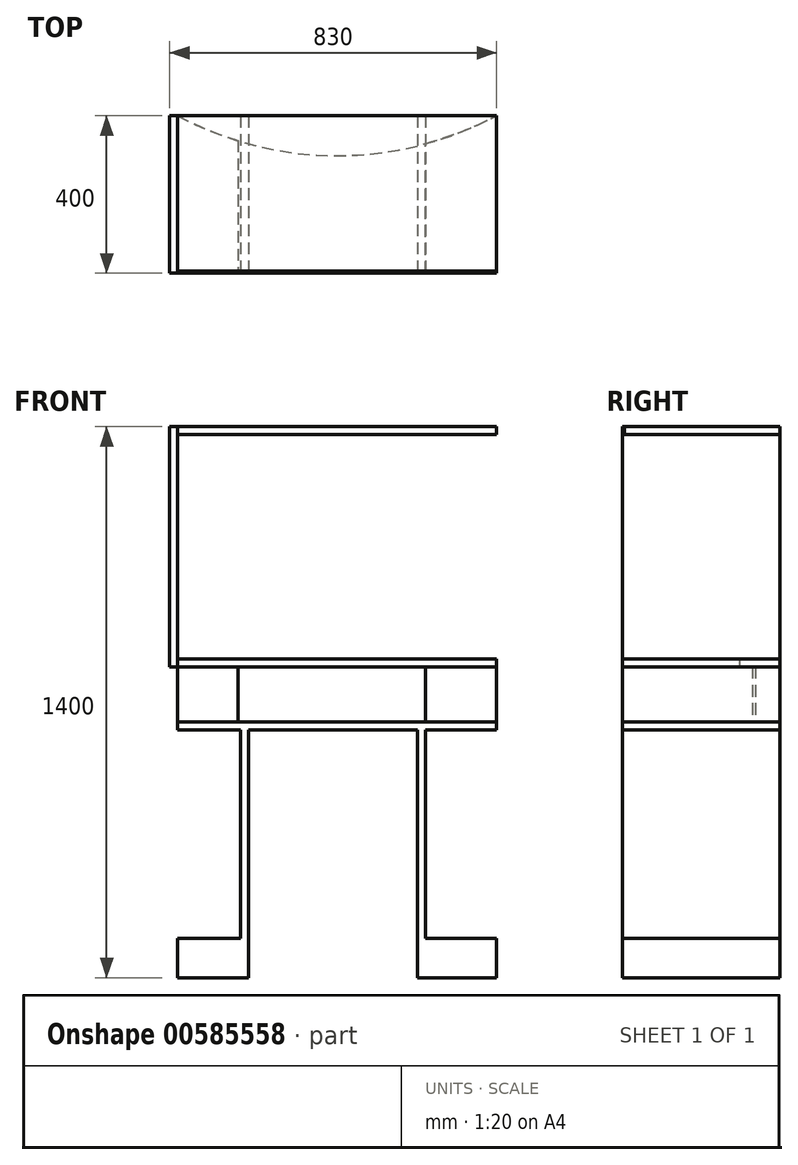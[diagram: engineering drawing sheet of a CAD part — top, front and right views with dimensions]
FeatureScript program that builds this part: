
annotation { "Feature Type Name" : "Feature", "Feature Type Description" : "" }
export const myFeature = defineFeature(function(context is Context, id is Id, definition is map)
    precondition{}
    {
        {
            var Q0;
            Q0=qCreatedBy(makeId("Front.planeOp"),FACE);
            var sketch = newSketch(context, id + "F0", { "sketchPlane" : qUnion([Q0])});
            skLineSegment(sketch, "E0.bottom", {"start": v(-650, -795.62) * mm, "end": v(200, -795.62) * mm});
            skLineSegment(sketch, "E0.top", {"start": v(-650, 604.38) * mm, "end": v(200, 604.38) * mm});
            skLineSegment(sketch, "E0.left", {"start": v(-650, -795.62) * mm, "end": v(-650, 604.38) * mm});
            skLineSegment(sketch, "E0.right", {"start": v(200, -795.62) * mm, "end": v(200, 604.38) * mm});
            skLineSegment(sketch, "E1.left", {"start": v(-650, 604.38) * mm, "end": v(-650, 534.38) * mm});
            skLineSegment(sketch, "E2", {"start": v(200, 604.38) * mm, "end": v(200, -795.62) * mm});
            skLineSegment(sketch, "E3", {"start": v(180, 604.38) * mm, "end": v(180, -795.62) * mm});
            skPoint(sketch, "E4.start.orphan", {"position": v(137.97, 604.38) * mm});
            skPoint(sketch, "E5.start.orphan", {"position": v(-630, 534.38) * mm});
            skLineSegment(sketch, "E6", {"start": v(180, -145.62) * mm, "end": v(-630, -145.62) * mm});
            skLineSegment(sketch, "E7", {"start": v(-630, -795.62) * mm, "end": v(-630, -145.62) * mm});
            skPoint(sketch, "E8.orphan", {"position": v(-610, 534.38) * mm});
            skLineSegment(sketch, "E9", {"start": v(-630, -145.62) * mm, "end": v(-630, 534.38) * mm});
            skLineSegment(sketch, "E10", {"start": v(-630, -165.62) * mm, "end": v(180, -165.62) * mm});
            skLineSegment(sketch, "E11", {"start": v(-630, -695.62) * mm, "end": v(180, -695.62) * mm});
            skLineSegment(sketch, "E12", {"start": v(-20, -795.62) * mm, "end": v(-20, -165.62) * mm});
            skLineSegment(sketch, "E13", {"start": v(0, -165.62) * mm, "end": v(0, -695.62) * mm});
            skLineSegment(sketch, "E14", {"start": v(-450, -165.62) * mm, "end": v(-450, -795.62) * mm});
            skLineSegment(sketch, "E15", {"start": v(-470, -165.62) * mm, "end": v(-470, -795.62) * mm});
            skLineSegment(sketch, "E16", {"start": v(0, -695.62) * mm, "end": v(0, -795.62) * mm});
            skLineSegment(sketch, "E17", {"start": v(180, 14.38) * mm, "end": v(-630, 14.38) * mm});
            skPoint(sketch, "E17.endSnap0", {"position": v(-630, 194.38) * mm});
            skLineSegment(sketch, "E18", {"start": v(-630, -5.62) * mm, "end": v(180, -5.62) * mm});
            skPoint(sketch, "E18.endSnap0", {"position": v(180, -95.62) * mm});
            skPoint(sketch, "E19.end.orphan", {"position": v(-590, 534.38) * mm});
            skLineSegment(sketch, "E20", {"start": v(-630, 534.38) * mm, "end": v(-630, 604.38) * mm});
            skLineSegment(sketch, "E21.top", {"start": v(-650, -5.62) * mm, "end": v(200, -5.62) * mm});
            skLineSegment(sketch, "E21.left", {"start": v(-650, 604.38) * mm, "end": v(-650, -5.62) * mm});
            skLineSegment(sketch, "E21.right", {"start": v(200, 604.38) * mm, "end": v(200, -5.62) * mm});
            skSolve(sketch);
        }
        {
            var Q0;
            {var subQ0=sQuery(id+"F0.wireOp",EDGE,"E14");var subQ1=sQuery(id+"F0.wireOp",EDGE,"E10");var subQ2=makeQuery(id+"F0.imprint","INTERSECT",VERTEX,{"derivedFrom":[subQ1,subQ0]});Q0=makeQuery(id+"F0.imprint","IMPRINT",FACE,{"disambiguationData":[TD([[makeQuery(id+"F0.imprint","IMPRINT",EDGE,{"disambiguationData":[TD([[subQ2,1.0]])],"derivedFrom":subQ1}),-1.0]])]});}
            var Q1;
            {var subQ3=sQuery(id+"F0.wireOp",EDGE,"E13");Q1=makeQuery(id+"F0.imprint","IMPRINT",FACE,{"disambiguationData":[TD([[makeQuery(id+"F0.imprint","IMPRINT",EDGE,{"derivedFrom":subQ3}),-1.0]])]});}
            var Q2;
            {var subQ1=sQuery(id+"F0.wireOp",EDGE,"E6");Q2=makeQuery(id+"F0.imprint","IMPRINT",FACE,{"disambiguationData":[TD([[makeQuery(id+"F0.imprint","IMPRINT",EDGE,{"derivedFrom":subQ1}),1.0]])]});}
            var Q3;
            {var subQ0=sQuery(id+"F0.wireOp",EDGE,"E7");var subQ1=sQuery(id+"F0.wireOp",EDGE,"E0.bottom");var subQ2=makeQuery(id+"F0.imprint","INTERSECT",VERTEX,{"derivedFrom":[subQ1,subQ0]});Q3=makeQuery(id+"F0.imprint","IMPRINT",FACE,{"disambiguationData":[TD([[makeQuery(id+"F0.imprint","IMPRINT",EDGE,{"disambiguationData":[TD([[subQ2,-1.0]])],"derivedFrom":subQ1}),1.0]])]});}
            var Q4;
            {var subQ0=sQuery(id+"F0.wireOp",EDGE,"E14");var subQ1=sQuery(id+"F0.wireOp",EDGE,"E0.bottom");var subQ2=makeQuery(id+"F0.imprint","INTERSECT",VERTEX,{"derivedFrom":[subQ1,subQ0]});Q4=makeQuery(id+"F0.imprint","IMPRINT",FACE,{"disambiguationData":[TD([[makeQuery(id+"F0.imprint","IMPRINT",EDGE,{"disambiguationData":[TD([[subQ2,1.0]])],"derivedFrom":subQ1}),1.0]])]});}
            var Q5;
            {var subQ3=sQuery(id+"F0.wireOp",EDGE,"E16");Q5=makeQuery(id+"F0.imprint","IMPRINT",FACE,{"disambiguationData":[TD([[makeQuery(id+"F0.imprint","IMPRINT",EDGE,{"derivedFrom":subQ3}),-1.0]])]});}
            var Q6;
            {var subQ3=sQuery(id+"F0.wireOp",EDGE,"E16");Q6=makeQuery(id+"F0.imprint","IMPRINT",FACE,{"disambiguationData":[TD([[makeQuery(id+"F0.imprint","IMPRINT",EDGE,{"derivedFrom":subQ3}),1.0]])]});}
            var Q7;
            {var subQ5=sQuery(id+"F0.wireOp",EDGE,"E0.left");Q7=makeQuery(id+"F0.imprint","IMPRINT",FACE,{"disambiguationData":[TD([[makeQuery(id+"F0.imprint","IMPRINT",EDGE,{"derivedFrom":subQ5}),-1.0]])]});}
            var Q8;
            {var subQ4=sQuery(id+"F0.wireOp",EDGE,"E2");Q8=makeQuery(id+"F0.imprint","IMPRINT",FACE,{"disambiguationData":[TD([[makeQuery(id+"F0.imprint","IMPRINT",EDGE,{"derivedFrom":subQ4}),-1.0]])]});}
            extrude(context, id + "F1", {"entities" : qUnion([Q0, Q1, Q2, Q3, Q4, Q5, Q6, Q7, Q8]), "oppositeDirection" : true, "depth" : 400 * mm, "offsetDistance" : 25.4 * mm});
        }
        {
            var Q0;
            Q0=makeQuery(id+"F1.opExtrude","SWEPT_FACE",FACE,{"disambiguationData":[OSD([sQuery(id+"F0.wireOp",EDGE,"E9"),sQuery(id+"F0.wireOp",EDGE,"E20")])]});
            var sketch = newSketch(context, id + "F2", { "sketchPlane" : qUnion([Q0])});
            skLineSegment(sketch, "E22.bottom", {"start": v(5.08, 584.38) * mm, "end": v(400, 584.38) * mm});
            skLineSegment(sketch, "E22.top", {"start": v(5.08, 604.38) * mm, "end": v(400, 604.38) * mm});
            skLineSegment(sketch, "E22.left", {"start": v(5.08, 584.38) * mm, "end": v(5.08, 604.38) * mm});
            skLineSegment(sketch, "E22.right", {"start": v(400, 584.38) * mm, "end": v(400, 604.38) * mm});
            skSolve(sketch);
        }
        {
            var Q0;
            {var subQ7=sQuery(id+"F2.wireOp",EDGE,"E22.bottom");Q0=makeQuery(id+"F2.imprint","IMPRINT",FACE,{"disambiguationData":[TD([[makeQuery(id+"F2.imprint","IMPRINT",EDGE,{"derivedFrom":subQ7}),1.0]])]});}
            extrude(context, id + "F3", {"entities" : qUnion([Q0]), "operationType" : NewBodyOperationType.ADD, "depth" : 810 * mm, "offsetDistance" : 25.4 * mm});
        }
        {
            var Q0;
            {var subQ0=sQuery(id+"F0.wireOp",EDGE,"E21.right");Q0=makeQuery(id+"F0.imprint","IMPRINT",FACE,{"disambiguationData":[TD([[makeQuery(id+"F0.imprint","IMPRINT",EDGE,{"derivedFrom":subQ0}),-1.0]])]});}
            var Q1;
            {var subQ1=sQuery(id+"F0.wireOp",EDGE,"E20");Q1=makeQuery(id+"F0.imprint","IMPRINT",FACE,{"disambiguationData":[TD([[makeQuery(id+"F0.imprint","IMPRINT",EDGE,{"derivedFrom":subQ1}),1.0]])]});}
            extrude(context, id + "F4", {"entities" : qUnion([Q0, Q1]), "oppositeDirection" : true, "depth" : 400 * mm, "offsetDistance" : 25.4 * mm});
        }
        {
            var Q0;
            {var subQ0=sQuery(id+"F0.wireOp",EDGE,"E17");Q0=makeQuery(id+"F0.imprint","IMPRINT",FACE,{"disambiguationData":[TD([[makeQuery(id+"F0.imprint","IMPRINT",EDGE,{"derivedFrom":subQ0}),-1.0]])]});}
            var sketch = newSketch(context, id + "F5", { "sketchPlane" : qUnion([Q0])});
            skSolve(sketch);
        }
        {
            var Q0;
            Q0 = qSketchRegion(id + "F5", true);
            var Q1;
            {var subQ0=sQuery(id+"F0.wireOp",EDGE,"E17");Q1=makeQuery(id+"F0.imprint","IMPRINT",FACE,{"disambiguationData":[TD([[makeQuery(id+"F0.imprint","IMPRINT",EDGE,{"derivedFrom":subQ0}),-1.0]])]});}
            extrude(context, id + "F6", {"entities" : qUnion([Q0, Q1]), "depth" : 20 * mm, "offsetDistance" : 25.4 * mm});
        }
        {
            var Q0;
            {var subQ0=sQuery(id+"F0.wireOp",EDGE,"E17");Q0=makeQuery(id+"F0.imprint","IMPRINT",FACE,{"disambiguationData":[TD([[makeQuery(id+"F0.imprint","IMPRINT",EDGE,{"derivedFrom":subQ0}),1.0]])]});}
            extrude(context, id + "F7", {"entities" : qUnion([Q0]), "oppositeDirection" : true, "depth" : 400 * mm, "offsetDistance" : 25.4 * mm});
        }
        {
            var Q0;
            Q0=makeQuery(id+"F7.opExtrude","SWEPT_FACE",FACE,{"disambiguationData":[OSD([sQuery(id+"F0.wireOp",EDGE,"E17")])]});
            var sketch = newSketch(context, id + "F8", { "sketchPlane" : qUnion([Q0])});
            skArc(sketch, "E23", {"start": v(-630, 400) * mm, "mid": v(-225, 298.46) * mm, "end": v(180, 400) * mm});
            skLineSegment(sketch, "E24", {"start": v(180, 400) * mm, "end": v(-630, 400) * mm});
            skSolve(sketch);
        }
        {
            var Q0;
            Q0=makeQuery(id+"F8.imprint","IMPRINT",FACE,{"disambiguationData":[TD([[makeQuery(id+"F8.imprint","IMPRINT",EDGE,{"derivedFrom":sQuery(id+"F8.wireOp",EDGE,"E23")}),1.0]])]});
            extrude(context, id + "F9", {"entities" : qUnion([Q0]), "operationType" : NewBodyOperationType.REMOVE, "oppositeDirection" : true, "depth" : 25.4 * mm, "offsetDistance" : 25.4 * mm});
        }
        {
            var Q0;
            Q0=makeQuery(id+"F1.opExtrude","SWEPT_FACE",FACE,{"disambiguationData":[OSD([sQuery(id+"F0.wireOp",EDGE,"E6")])]});
            var sketch = newSketch(context, id + "F10", { "sketchPlane" : qUnion([Q0])});
            skArc(sketch, "E25", {"start": v(-630, 400) * mm, "mid": v(-225, 300.8) * mm, "end": v(180, 400) * mm});
            skLineSegment(sketch, "E26", {"start": v(-476.1, 337.54) * mm, "end": v(-476.1, 0) * mm});
            skLineSegment(sketch, "E27", {"start": v(-476.1, 0) * mm, "end": v(-630, 0) * mm});
            skLineSegment(sketch, "E28", {"start": v(-630, 0) * mm, "end": v(-630, 400) * mm});
            skLineSegment(sketch, "E29", {"start": v(180, 400) * mm, "end": v(180, 0) * mm});
            skLineSegment(sketch, "E30", {"start": v(180, 0) * mm, "end": v(0, 0) * mm});
            skLineSegment(sketch, "E31", {"start": v(0, 0) * mm, "end": v(0, 330.17) * mm});
            skSolve(sketch);
        }
        {
            var Q0;
            {var subQ0=sQuery(id+"F10.wireOp",EDGE,"E29");Q0=makeQuery(id+"F10.imprint","IMPRINT",FACE,{"disambiguationData":[TD([[makeQuery(id+"F10.imprint","IMPRINT",EDGE,{"derivedFrom":subQ0}),-1.0]])]});}
            var Q1;
            {var subQ2=sQuery(id+"F10.wireOp",EDGE,"E26");Q1=makeQuery(id+"F10.imprint","IMPRINT",FACE,{"disambiguationData":[TD([[makeQuery(id+"F10.imprint","IMPRINT",EDGE,{"derivedFrom":subQ2}),-1.0]])]});}
            extrude(context, id + "F11", {"entities" : qUnion([Q0, Q1]), "depth" : 140 * mm, "offsetDistance" : 25.4 * mm});
        }
        {
            var Q0;
            Q0=makeQuery(id+"F6.opExtrude","SWEPT_BODY",BODY,{"disambiguationData":[OSD([sQuery(id+"F0.wireOp",EDGE,"E3"),sQuery(id+"F0.wireOp",EDGE,"E9"),sQuery(id+"F0.wireOp",EDGE,"E17"),sQuery(id+"F0.wireOp",EDGE,"E20"),sQuery(id+"F0.wireOp",EDGE,"E0.top")])]});
            deleteBodies(context, id + "F12", {"entities" : qUnion([Q0])});
        }
    });
